SOLIDWORKS PART (.sldprt)
format: sldprt  version: not decoded by parser v0  size: 183,808 bytes
history: native  units: mm
features: sketch x5, plane x3, extrude x2, cut_extrude x2, material x1, revolve x1 (+13 scaffold rows collapsed)
feature tree (27):
  scaffold x13  (default folders/planes/origin — collapsed)
  material  "材质 <未指定>"
  plane  "前视基准面"
  plane  "上视基准面"
  plane  "右视基准面"
  sketch  "草图1"  dims[D1=~8.687019mm]
  revolve  "旋转1"  Angle=20deg
  sketch  "草图2"
  extrude  "凸台-拉伸1"  Depth=10mm
  sketch  "草图3"  dims[c1.D2=80.0deg c2.D2=15.0mm c2.D3=15.0mm c2.D1=20.0mm c3.D2=15.0mm c3.D1=0.0mm c3.D4=0.5mm c3.D5=0.5mm]
  extrude  "凸台-拉伸2"  Depth=360mm
  sketch  "草图4"
  cut_extrude  "切除-拉伸1"  [1 undecoded]
  sketch  "草图5"
  cut_extrude  "切除-拉伸2"  [1 undecoded]
decode coverage: 5 of 10 modeling features carry decoded parameters
note: ~ marks probable driven/reference dimensions
note: 2 parameter values undecoded
note: suppression state not decoded; provenance and decode notes live in map.json
